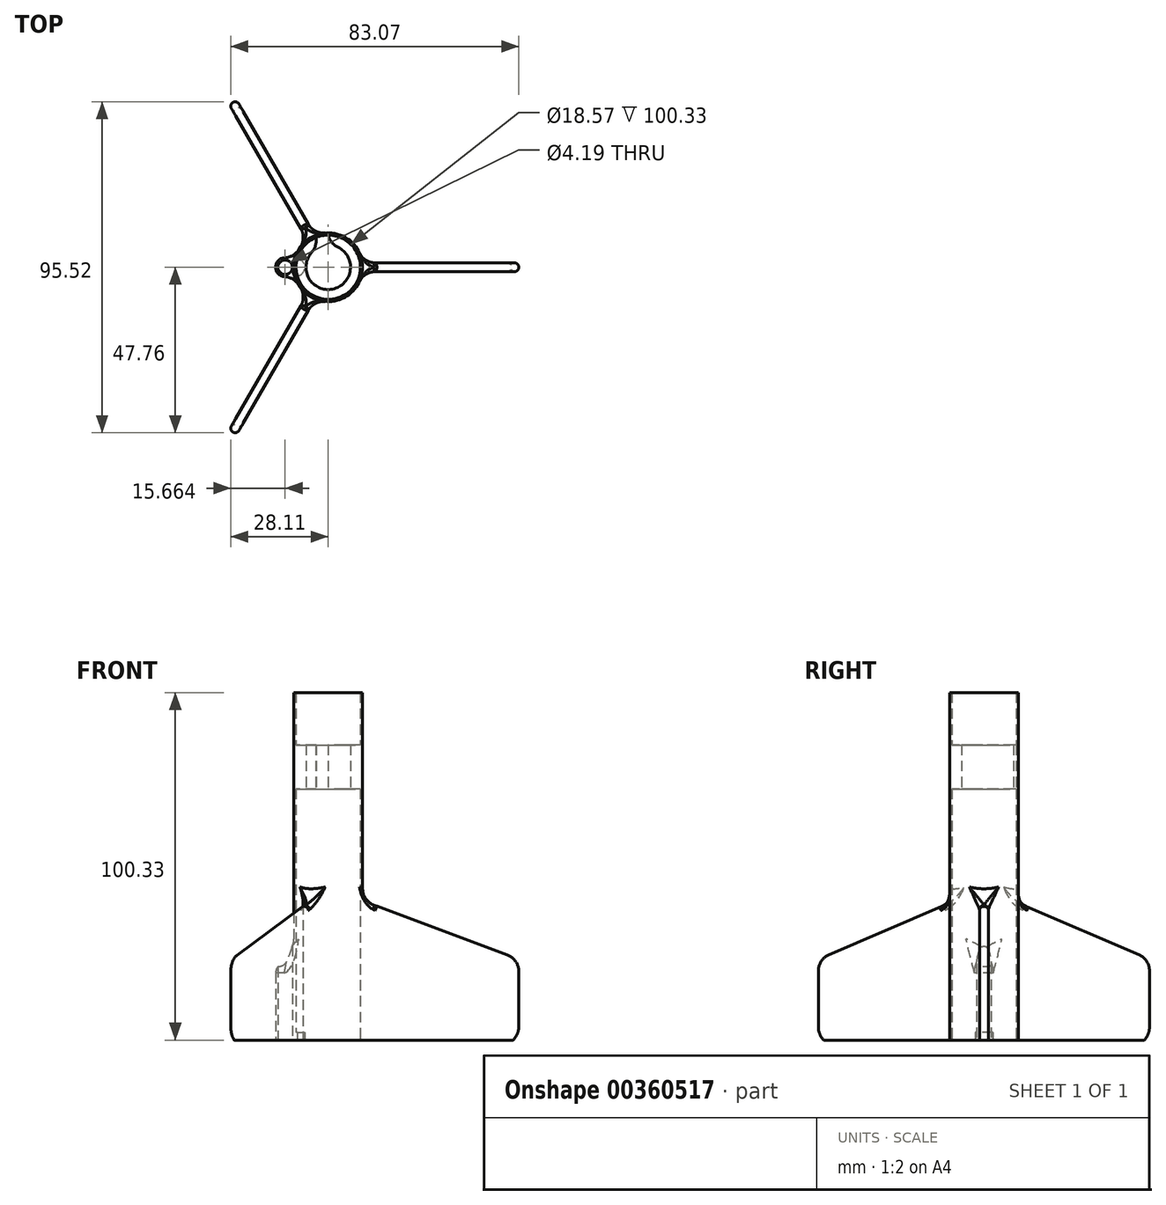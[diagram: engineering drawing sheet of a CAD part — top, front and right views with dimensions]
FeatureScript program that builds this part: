
annotation { "Feature Type Name" : "Feature", "Feature Type Description" : "" }
export const myFeature = defineFeature(function(context is Context, id is Id, definition is map)
    precondition{}
    {
        {
            var Q0;
            Q0=qCreatedBy(makeId("Top.planeOp"),FACE);
            var sketch = newSketch(context, id + "F0", { "sketchPlane" : qUnion([Q0])});
            skCircle(sketch, "E0", {"center": v(0, 0) * mm, "radius": 9.28 * mm});
            skCircle(sketch, "E1", {"center": v(0, 0) * mm, "radius": 9.92 * mm});
            skSolve(sketch);
        }
        {
            var Q0;
            Q0 = qSketchRegion(id + "F0", true);
            extrude(context, id + "F1", {"entities" : qUnion([Q0]), "depth" : 101.6 * mm});
        }
        {
            var Q0;
            Q0=qCreatedBy(makeId("Front.planeOp"),FACE);
            var sketch = newSketch(context, id + "F2", { "sketchPlane" : qUnion([Q0])});
            skLineSegment(sketch, "E2", {"start": v(0, 45.13) * mm, "end": v(54.96, 24.63) * mm});
            skLineSegment(sketch, "E3", {"start": v(54.96, 24.63) * mm, "end": v(54.96, 0) * mm});
            skLineSegment(sketch, "E4", {"start": v(54.96, 0) * mm, "end": v(0, 0) * mm});
            skLineSegment(sketch, "E5", {"start": v(0, 0) * mm, "end": v(0, 45.13) * mm});
            skSolve(sketch);
        }
        {
            var Q0;
            Q0 = qSketchRegion(id + "F2", true);
            extrude(context, id + "F3", {"entities" : qUnion([Q0]), "operationType" : NewBodyOperationType.ADD, "depth" : 1.27 * mm, "hasSecondDirection" : true, "secondDirectionOppositeDirection" : true, "secondDirectionDepth" : 1.27 * mm});
        }
        {
            var Q0;
            Q0=makeQuery(id+"F6.opPattern","COPY",EDGE,{"derivedFrom":makeQuery(id+"F3.boolean.opBoolean","INTERSECT",EDGE,{"derivedFrom":[makeQuery(id+"F1.opExtrude","SWEPT_FACE",FACE,{"disambiguationData":[OSD([sQuery(id+"F0.wireOp",EDGE,"E1")])]}),makeQuery(id+"F3.opExtrude","CAP_FACE",FACE,{"disambiguationData":[OSD([sQuery(id+"F2.wireOp",EDGE,"E2"),sQuery(id+"F2.wireOp",EDGE,"E3"),sQuery(id+"F2.wireOp",EDGE,"E4"),sQuery(id+"F2.wireOp",EDGE,"E5")])],"isStart":true})]}),"instanceName":"1"});
            var Q1;
            Q1=makeQuery(id+"F6.opPattern","COPY",EDGE,{"derivedFrom":makeQuery(id+"F3.boolean.opBoolean","INTERSECT",EDGE,{"derivedFrom":[makeQuery(id+"F1.opExtrude","SWEPT_FACE",FACE,{"disambiguationData":[OSD([sQuery(id+"F0.wireOp",EDGE,"E1")])]}),makeQuery(id+"F3.opExtrude","CAP_FACE",FACE,{"disambiguationData":[OSD([sQuery(id+"F2.wireOp",EDGE,"E2"),sQuery(id+"F2.wireOp",EDGE,"E3"),sQuery(id+"F2.wireOp",EDGE,"E4"),sQuery(id+"F2.wireOp",EDGE,"E5")])],"isStart":false})]}),"instanceName":"2"});
            var Q2;
            Q2=makeQuery(id+"F6.opPattern","COPY",EDGE,{"derivedFrom":makeQuery(id+"F3.boolean.opBoolean","INTERSECT",EDGE,{"derivedFrom":[makeQuery(id+"F1.opExtrude","SWEPT_FACE",FACE,{"disambiguationData":[OSD([sQuery(id+"F0.wireOp",EDGE,"E1")])]}),makeQuery(id+"F3.opExtrude","CAP_FACE",FACE,{"disambiguationData":[OSD([sQuery(id+"F2.wireOp",EDGE,"E2"),sQuery(id+"F2.wireOp",EDGE,"E3"),sQuery(id+"F2.wireOp",EDGE,"E4"),sQuery(id+"F2.wireOp",EDGE,"E5")])],"isStart":true})]}),"instanceName":"2"});
            var Q3;
            Q3=makeQuery(id+"F3.boolean.opBoolean","INTERSECT",EDGE,{"derivedFrom":[makeQuery(id+"F1.opExtrude","SWEPT_FACE",FACE,{"disambiguationData":[OSD([sQuery(id+"F0.wireOp",EDGE,"E1")])]}),makeQuery(id+"F3.opExtrude","CAP_FACE",FACE,{"disambiguationData":[OSD([sQuery(id+"F2.wireOp",EDGE,"E2"),sQuery(id+"F2.wireOp",EDGE,"E3"),sQuery(id+"F2.wireOp",EDGE,"E4"),sQuery(id+"F2.wireOp",EDGE,"E5")])],"isStart":false})]});
            var Q4;
            Q4=makeQuery(id+"F3.boolean.opBoolean","INTERSECT",EDGE,{"derivedFrom":[makeQuery(id+"F1.opExtrude","SWEPT_FACE",FACE,{"disambiguationData":[OSD([sQuery(id+"F0.wireOp",EDGE,"E1")])]}),makeQuery(id+"F3.opExtrude","CAP_FACE",FACE,{"disambiguationData":[OSD([sQuery(id+"F2.wireOp",EDGE,"E2"),sQuery(id+"F2.wireOp",EDGE,"E3"),sQuery(id+"F2.wireOp",EDGE,"E4"),sQuery(id+"F2.wireOp",EDGE,"E5")])],"isStart":true})]});
            var Q5;
            Q5=makeQuery(id+"F6.opPattern","COPY",EDGE,{"derivedFrom":makeQuery(id+"F3.boolean.opBoolean","INTERSECT",EDGE,{"derivedFrom":[makeQuery(id+"F1.opExtrude","SWEPT_FACE",FACE,{"disambiguationData":[OSD([sQuery(id+"F0.wireOp",EDGE,"E1")])]}),makeQuery(id+"F3.opExtrude","CAP_FACE",FACE,{"disambiguationData":[OSD([sQuery(id+"F2.wireOp",EDGE,"E2"),sQuery(id+"F2.wireOp",EDGE,"E3"),sQuery(id+"F2.wireOp",EDGE,"E4"),sQuery(id+"F2.wireOp",EDGE,"E5")])],"isStart":false})]}),"instanceName":"1"});
            var Q6;
            Q6=makeQuery(id+"F3.opExtrude","SWEPT_EDGE",EDGE,{"disambiguationData":[OSD([sQuery(id+"F2.wireOp",EDGE,"E2"),sQuery(id+"F2.wireOp",EDGE,"E3")])]});
            var Q7;
            Q7=makeQuery(id+"F6.opPattern","COPY",EDGE,{"derivedFrom":makeQuery(id+"F3.opExtrude","SWEPT_EDGE",EDGE,{"disambiguationData":[OSD([sQuery(id+"F2.wireOp",EDGE,"E2"),sQuery(id+"F2.wireOp",EDGE,"E3")])]}),"instanceName":"2"});
            var Q8;
            Q8=makeQuery(id+"F6.opPattern","COPY",EDGE,{"derivedFrom":makeQuery(id+"F3.opExtrude","SWEPT_EDGE",EDGE,{"disambiguationData":[OSD([sQuery(id+"F2.wireOp",EDGE,"E2"),sQuery(id+"F2.wireOp",EDGE,"E3")])]}),"instanceName":"1"});
            var Q9;
            Q9=makeQuery(id+"F3.opExtrude","SWEPT_EDGE",EDGE,{"disambiguationData":[OSD([sQuery(id+"F2.wireOp",EDGE,"E3"),sQuery(id+"F2.wireOp",EDGE,"E4")])]});
            var Q10;
            Q10=makeQuery(id+"F6.opPattern","COPY",EDGE,{"derivedFrom":makeQuery(id+"F3.opExtrude","SWEPT_EDGE",EDGE,{"disambiguationData":[OSD([sQuery(id+"F2.wireOp",EDGE,"E3"),sQuery(id+"F2.wireOp",EDGE,"E4")])]}),"instanceName":"1"});
            var Q11;
            Q11=makeQuery(id+"F6.opPattern","COPY",EDGE,{"derivedFrom":makeQuery(id+"F3.opExtrude","SWEPT_EDGE",EDGE,{"disambiguationData":[OSD([sQuery(id+"F2.wireOp",EDGE,"E3"),sQuery(id+"F2.wireOp",EDGE,"E4")])]}),"instanceName":"2"});
            var Q12;
            Q12=makeQuery(id+"F6.opPattern","COPY",EDGE,{"derivedFrom":makeQuery(id+"F3.boolean.opBoolean","INTERSECT",EDGE,{"derivedFrom":[makeQuery(id+"F1.opExtrude","SWEPT_FACE",FACE,{"disambiguationData":[OSD([sQuery(id+"F0.wireOp",EDGE,"E1")])]}),makeQuery(id+"F3.opExtrude","SWEPT_FACE",FACE,{"disambiguationData":[OSD([sQuery(id+"F2.wireOp",EDGE,"E2")])]})]}),"instanceName":"2"});
            var Q13;
            Q13=makeQuery(id+"F3.boolean.opBoolean","INTERSECT",EDGE,{"derivedFrom":[makeQuery(id+"F1.opExtrude","SWEPT_FACE",FACE,{"disambiguationData":[OSD([sQuery(id+"F0.wireOp",EDGE,"E1")])]}),makeQuery(id+"F3.opExtrude","SWEPT_FACE",FACE,{"disambiguationData":[OSD([sQuery(id+"F2.wireOp",EDGE,"E2")])]})]});
            var Q14;
            Q14=makeQuery(id+"F6.opPattern","COPY",EDGE,{"derivedFrom":makeQuery(id+"F3.boolean.opBoolean","INTERSECT",EDGE,{"derivedFrom":[makeQuery(id+"F1.opExtrude","SWEPT_FACE",FACE,{"disambiguationData":[OSD([sQuery(id+"F0.wireOp",EDGE,"E1")])]}),makeQuery(id+"F3.opExtrude","SWEPT_FACE",FACE,{"disambiguationData":[OSD([sQuery(id+"F2.wireOp",EDGE,"E2")])]})]}),"instanceName":"1"});
            fillet(context, id + "F4", {"entities" : qUnion([Q0, Q1, Q2, Q3, Q4, Q5, Q6, Q7, Q8, Q9, Q10, Q11, Q12, Q13, Q14]), "radius" : 5.08 * mm, "tangentPropagation" : true, "allowEdgeOverflow" : false});
        }
        {
            var Q0;
            {var subQ0=sQuery(id+"F2.wireOp",EDGE,"E2");Q0=makeQuery(id+"F3.boolean.opBoolean","SPLIT",EDGE,{"disambiguationData":[TD([makeQuery(id+"F1.opExtrude","SWEPT_FACE",FACE,{"disambiguationData":[OSD([sQuery(id+"F0.wireOp",EDGE,"E1")])]})])],"derivedFrom":makeQuery(id+"F3.opExtrude","CAP_EDGE",EDGE,{"disambiguationData":[OSD([subQ0])],"isStart":true})});}
            fillet(context, id + "F5", {"entities" : qUnion([Q0]), "radius" : 1.27 * mm, "tangentPropagation" : true, "allowEdgeOverflow" : false});
        }
        {
            var Q0;
            Q0=makeQuery(id+"F1.opExtrude","SWEPT_BODY",BODY,{"disambiguationData":[OSD([sQuery(id+"F0.wireOp",EDGE,"E0"),sQuery(id+"F0.wireOp",EDGE,"E1")])]});
            var Q1;
            Q1=makeQuery(id+"F1.opExtrude","SWEPT_FACE",FACE,{"disambiguationData":[OSD([sQuery(id+"F0.wireOp",EDGE,"E0")])]});
            circularPattern(context, id + "F6", {"operationType" : NewBodyOperationType.ADD, "entities" : qUnion([Q0]), "axis" : qUnion([Q1]), "angle" : 360 * degree, "instanceCount" : 3, "equalSpace" : true});
        }
        {
            var Q0;
            Q0=makeQuery(id+"F1.opExtrude","CAP_FACE",FACE,{"disambiguationData":[OSD([sQuery(id+"F0.wireOp",EDGE,"E0"),sQuery(id+"F0.wireOp",EDGE,"E1")])],"isStart":false});
            var sketch = newSketch(context, id + "F7", { "sketchPlane" : qUnion([Q0])});
            skCircle(sketch, "E6.0", {"center": v(0, 0) * mm, "radius": 9.28 * mm});
            skSolve(sketch);
        }
        {
            var Q0;
            Q0 = qSketchRegion(id + "F7", true);
            var Q1;
            {var subQ0=makeQuery(id+"F3.boolean.opBoolean","MERGE",FACE,{"derivedFrom":[makeQuery(id+"F1.opExtrude","CAP_FACE",FACE,{"disambiguationData":[OSD([sQuery(id+"F0.wireOp",EDGE,"E0"),sQuery(id+"F0.wireOp",EDGE,"E1")])],"isStart":true}),makeQuery(id+"F3.opExtrude","SWEPT_FACE",FACE,{"disambiguationData":[OSD([sQuery(id+"F2.wireOp",EDGE,"E4")])]})]});Q1=makeQuery(id+"F6.boolean.opBoolean","MERGE",FACE,{"derivedFrom":[subQ0,makeQuery(id+"F6.opPattern","COPY",FACE,{"derivedFrom":subQ0,"instanceName":"1"}),makeQuery(id+"F6.opPattern","COPY",FACE,{"derivedFrom":subQ0,"instanceName":"2"})]});}
            extrude(context, id + "F8", {"entities" : qUnion([Q0]), "operationType" : NewBodyOperationType.REMOVE, "endBound" : BoundingType.UP_TO_SURFACE, "oppositeDirection" : true, "endBoundEntityFace" : qUnion([Q1]), "depth" : 25.4 * mm});
        }
        {
            var Q0;
            Q0=qCreatedBy(makeId("Top.planeOp"),FACE);
            cPlane(context, id + "F9", {"entities" : qUnion([Q0]), "cplaneType" : CPlaneType.OFFSET, "offset" : 73.8 * mm, "width" : 152.4 * mm, "height" : 152.4 * mm});
        }
        {
            var Q0;
            Q0=qCreatedBy(id+"F9.planeOp",FACE);
            var sketch = newSketch(context, id + "F10", { "sketchPlane" : qUnion([Q0])});
            skCircle(sketch, "E7.0", {"center": v(0, 0) * mm, "radius": 9.28 * mm});
            skCircle(sketch, "E8", {"center": v(0, 0) * mm, "radius": 6.43 * mm});
            skSolve(sketch);
        }
        {
            var Q0;
            Q0 = qSketchRegion(id + "F10", true);
            extrude(context, id + "F11", {"entities" : qUnion([Q0]), "operationType" : NewBodyOperationType.ADD, "depth" : 12.7 * mm});
        }
        {
            var Q0;
            Q0=qCreatedBy(id+"F9.planeOp",FACE);
            var sketch = newSketch(context, id + "F12", { "sketchPlane" : qUnion([Q0])});
            skArc(sketch, "E9.0", {"start": v(0, 9.28) * mm, "mid": v(-1.82, 9.1) * mm, "end": v(-3.57, 8.57) * mm});
            skLineSegment(sketch, "E10", {"start": v(0, 0) * mm, "end": v(0, 9.28) * mm});
            skLineSegment(sketch, "E11", {"start": v(0, 0) * mm, "end": v(-3.57, 8.57) * mm});
            skSolve(sketch);
        }
        {
            var Q0;
            Q0 = qSketchRegion(id + "F12", true);
            var Q1;
            Q1=makeQuery(id+"F11.opExtrude","CAP_FACE",FACE,{"disambiguationData":[OSD([sQuery(id+"F10.wireOp",EDGE,"E7.0"),sQuery(id+"F10.wireOp",EDGE,"E8")])],"isStart":false});
            extrude(context, id + "F13", {"entities" : qUnion([Q0]), "operationType" : NewBodyOperationType.REMOVE, "endBound" : BoundingType.UP_TO_SURFACE, "endBoundEntityFace" : qUnion([Q1]), "depth" : 25.4 * mm});
        }
        {
            var Q0;
            Q0=makeQuery(id+"F13.boolean.opBoolean","COPY",EDGE,{"derivedFrom":makeQuery(id+"F13.opExtrude","CAP_EDGE",EDGE,{"disambiguationData":[OSD([sQuery(id+"F12.wireOp",EDGE,"E10")])],"isStart":false})});
            var Q1;
            Q1=makeQuery(id+"F13.boolean.opBoolean","COPY",EDGE,{"derivedFrom":makeQuery(id+"F13.opExtrude","CAP_EDGE",EDGE,{"disambiguationData":[OSD([sQuery(id+"F12.wireOp",EDGE,"E11")])],"isStart":false})});
            var Q2;
            Q2=makeQuery(id+"F13.boolean.opBoolean","INTERSECT",EDGE,{"derivedFrom":[makeQuery(id+"F11.opExtrude","SWEPT_FACE",FACE,{"disambiguationData":[OSD([sQuery(id+"F10.wireOp",EDGE,"E8")])]}),makeQuery(id+"F13.opExtrude","SWEPT_FACE",FACE,{"disambiguationData":[OSD([sQuery(id+"F12.wireOp",EDGE,"E10")])]})]});
            var Q3;
            Q3=makeQuery(id+"F13.boolean.opBoolean","INTERSECT",EDGE,{"derivedFrom":[makeQuery(id+"F11.opExtrude","SWEPT_FACE",FACE,{"disambiguationData":[OSD([sQuery(id+"F10.wireOp",EDGE,"E8")])]}),makeQuery(id+"F13.opExtrude","SWEPT_FACE",FACE,{"disambiguationData":[OSD([sQuery(id+"F12.wireOp",EDGE,"E11")])]})]});
            var Q4;
            Q4=makeQuery(id+"F13.boolean.opBoolean","COPY",EDGE,{"derivedFrom":makeQuery(id+"F13.opExtrude","CAP_EDGE",EDGE,{"disambiguationData":[OSD([sQuery(id+"F12.wireOp",EDGE,"E10")])],"isStart":true})});
            var Q5;
            Q5=makeQuery(id+"F13.boolean.opBoolean","COPY",EDGE,{"derivedFrom":makeQuery(id+"F13.opExtrude","CAP_EDGE",EDGE,{"disambiguationData":[OSD([sQuery(id+"F12.wireOp",EDGE,"E11")])],"isStart":true})});
            fillet(context, id + "F14", {"entities" : qUnion([Q0, Q1, Q2, Q3, Q4, Q5]), "radius" : 5.08 * mm, "tangentPropagation" : true, "allowEdgeOverflow" : false});
        }
        {
            var Q0;
            Q0=qCreatedBy(makeId("Top.planeOp"),FACE);
            var sketch = newSketch(context, id + "F15", { "sketchPlane" : qUnion([Q0])});
            skCircle(sketch, "E12", {"center": v(-12.45, 0) * mm, "radius": 2.1 * mm});
            skCircle(sketch, "E13", {"center": v(-12.45, 0) * mm, "radius": 2.73 * mm});
            skSolve(sketch);
        }
        {
            var Q0;
            Q0 = qSketchRegion(id + "F15", true);
            extrude(context, id + "F16", {"entities" : qUnion([Q0]), "operationType" : NewBodyOperationType.ADD, "depth" : 25.4 * mm});
        }
        {
            var Q0;
            Q0=makeQuery(id+"F16.boolean.opBoolean","INTERSECT",EDGE,{"disambiguationData":[OD(1.0)],"derivedFrom":[makeQuery(id+"F1.opExtrude","SWEPT_FACE",FACE,{"disambiguationData":[OSD([sQuery(id+"F0.wireOp",EDGE,"E1")])]}),makeQuery(id+"F16.opExtrude","SWEPT_FACE",FACE,{"disambiguationData":[OSD([sQuery(id+"F15.wireOp",EDGE,"E13")])]})]});
            var Q1;
            Q1=makeQuery(id+"F16.boolean.opBoolean","INTERSECT",EDGE,{"derivedFrom":[makeQuery(id+"F1.opExtrude","SWEPT_FACE",FACE,{"disambiguationData":[OSD([sQuery(id+"F0.wireOp",EDGE,"E1")])]}),makeQuery(id+"F16.opExtrude","CAP_FACE",FACE,{"disambiguationData":[OSD([sQuery(id+"F15.wireOp",EDGE,"E12"),sQuery(id+"F15.wireOp",EDGE,"E13")])],"isStart":false})]});
            fillet(context, id + "F17", {"entities" : qUnion([Q0, Q1]), "radius" : 5.08 * mm, "tangentPropagation" : true, "allowEdgeOverflow" : false});
        }
        {
            var Q0;
            Q0=qCreatedBy(makeId("Top.planeOp"),FACE);
            cPlane(context, id + "F18", {"entities" : qUnion([Q0]), "cplaneType" : CPlaneType.OFFSET, "offset" : 1.27 * mm, "width" : 152.4 * mm, "height" : 152.4 * mm});
        }
        {
            var Q0;
            Q0=qCreatedBy(id+"F18.planeOp",FACE);
            var sketch = newSketch(context, id + "F19", { "sketchPlane" : qUnion([Q0])});
            skLineSegment(sketch, "E14.bottom", {"start": v(-59.53, -61.52) * mm, "end": v(59.53, -61.52) * mm});
            skLineSegment(sketch, "E14.top", {"start": v(-59.53, 62.12) * mm, "end": v(59.53, 62.12) * mm});
            skLineSegment(sketch, "E14.left", {"start": v(-59.53, -61.52) * mm, "end": v(-59.53, 62.12) * mm});
            skLineSegment(sketch, "E14.right", {"start": v(59.53, -61.52) * mm, "end": v(59.53, 62.12) * mm});
            skPoint(sketch, "E14.middle", {"position": v(0, 0.3) * mm});
            skSolve(sketch);
        }
        {
            var Q0;
            Q0 = qSketchRegion(id + "F19", true);
            extrude(context, id + "F20", {"entities" : qUnion([Q0]), "operationType" : NewBodyOperationType.REMOVE, "oppositeDirection" : true, "depth" : 25.4 * mm});
        }
        {
            var Q0;
            Q0=makeQuery(id+"F16.opExtrude","CAP_EDGE",EDGE,{"disambiguationData":[OSD([sQuery(id+"F15.wireOp",EDGE,"E13")])],"isStart":false});
            fillet(context, id + "F21", {"entities" : qUnion([Q0]), "radius" : 5.08 * mm, "tangentPropagation" : true, "allowEdgeOverflow" : false});
        }
        {
            var Q0;
            Q0=qCreatedBy(id+"F18.planeOp",FACE);
            var sketch = newSketch(context, id + "F22", { "sketchPlane" : qUnion([Q0])});
            skArc(sketch, "E15.0", {"start": v(-8.94, 2.52) * mm, "mid": v(-9.28, 0) * mm, "end": v(-8.94, -2.52) * mm});
            skArc(sketch, "E16", {"start": v(-8.94, -2.52) * mm, "mid": v(-6.74, 0) * mm, "end": v(-8.94, 2.52) * mm});
            skSolve(sketch);
        }
        {
            var Q0;
            Q0 = qSketchRegion(id + "F22", true);
            extrude(context, id + "F23", {"entities" : qUnion([Q0]), "operationType" : NewBodyOperationType.ADD, "depth" : 2.3 * mm});
        }
    });
